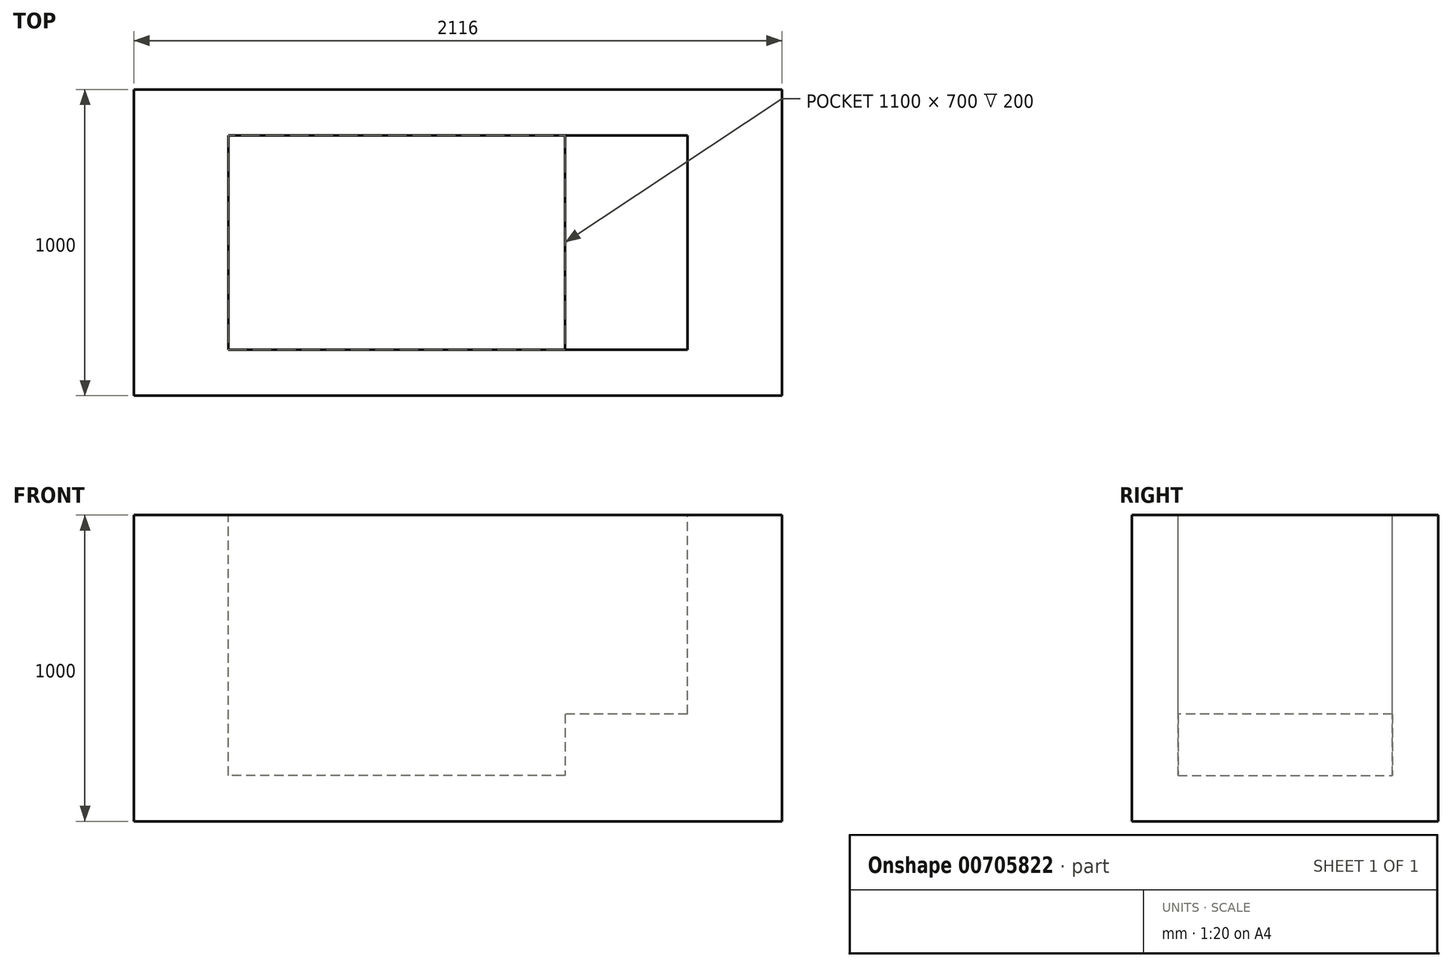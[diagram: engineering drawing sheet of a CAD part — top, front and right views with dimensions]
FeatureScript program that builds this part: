
annotation { "Feature Type Name" : "Feature", "Feature Type Description" : "" }
export const myFeature = defineFeature(function(context is Context, id is Id, definition is map)
    precondition{}
    {
        {
            var Q0;
            Q0=qCreatedBy(makeId("Top.planeOp"),FACE);
            var sketch = newSketch(context, id + "F0", { "sketchPlane" : qUnion([Q0])});
            skLineSegment(sketch, "E0.bottom", {"start": v(-110.6, -36.4) * mm, "end": v(2005.4, -36.4) * mm});
            skLineSegment(sketch, "E0.top", {"start": v(-110.6, 963.6) * mm, "end": v(2005.4, 963.6) * mm});
            skLineSegment(sketch, "E0.left", {"start": v(-110.6, -36.4) * mm, "end": v(-110.6, 963.6) * mm});
            skLineSegment(sketch, "E0.right", {"start": v(2005.4, -36.4) * mm, "end": v(2005.4, 963.6) * mm});
            skSolve(sketch);
        }
        {
            var Q0;
            Q0=makeQuery(id+"F0.imprint","IMPRINT",FACE,{"disambiguationData":[TD([[makeQuery(id+"F0.imprint","IMPRINT",EDGE,{"derivedFrom":sQuery(id+"F0.wireOp",EDGE,"E0.bottom")}),1.0]])]});
            extrude(context, id + "F1", {"entities" : qUnion([Q0]), "depth" : 1000 * mm, "offsetDistance" : 25 * mm});
        }
        {
            var Q0;
            Q0=makeQuery(id+"F1.opExtrude","CAP_FACE",FACE,{"disambiguationData":[OSD([sQuery(id+"F0.wireOp",EDGE,"E0.bottom"),sQuery(id+"F0.wireOp",EDGE,"E0.top"),sQuery(id+"F0.wireOp",EDGE,"E0.left"),sQuery(id+"F0.wireOp",EDGE,"E0.right")])],"isStart":false});
            var sketch = newSketch(context, id + "F2", { "sketchPlane" : qUnion([Q0])});
            skLineSegment(sketch, "E1.bottom", {"start": v(1697.4, 813.6) * mm, "end": v(197.4, 813.6) * mm});
            skLineSegment(sketch, "E1.top", {"start": v(1697.4, 113.6) * mm, "end": v(197.4, 113.6) * mm});
            skLineSegment(sketch, "E1.left", {"start": v(1697.4, 813.6) * mm, "end": v(1697.4, 113.6) * mm});
            skLineSegment(sketch, "E1.right", {"start": v(197.4, 813.6) * mm, "end": v(197.4, 113.6) * mm});
            skSolve(sketch);
        }
        {
            var Q0;
            Q0=makeQuery(id+"F2.imprint","IMPRINT",FACE,{"disambiguationData":[TD([[makeQuery(id+"F2.imprint","IMPRINT",EDGE,{"derivedFrom":sQuery(id+"F2.wireOp",EDGE,"E1.bottom")}),1.0]])]});
            extrude(context, id + "F3", {"entities" : qUnion([Q0]), "operationType" : NewBodyOperationType.REMOVE, "oppositeDirection" : true, "depth" : 850 * mm, "offsetDistance" : 25 * mm});
        }
        {
            var Q0;
            Q0=makeQuery(id+"F3.boolean.opBoolean","COPY",FACE,{"derivedFrom":makeQuery(id+"F3.opExtrude","CAP_FACE",FACE,{"disambiguationData":[OSD([sQuery(id+"F2.wireOp",EDGE,"E1.bottom"),sQuery(id+"F2.wireOp",EDGE,"E1.top"),sQuery(id+"F2.wireOp",EDGE,"E1.left"),sQuery(id+"F2.wireOp",EDGE,"E1.right")])],"isStart":false})});
            var sketch = newSketch(context, id + "F4", { "sketchPlane" : qUnion([Q0])});
            skLineSegment(sketch, "E2.bottom", {"start": v(1697.4, 113.6) * mm, "end": v(1297.4, 113.6) * mm});
            skLineSegment(sketch, "E2.top", {"start": v(1697.4, 813.6) * mm, "end": v(1297.4, 813.6) * mm});
            skLineSegment(sketch, "E2.left", {"start": v(1697.4, 113.6) * mm, "end": v(1697.4, 813.6) * mm});
            skLineSegment(sketch, "E2.right", {"start": v(1297.4, 113.6) * mm, "end": v(1297.4, 813.6) * mm});
            skSolve(sketch);
        }
        {
            var Q0;
            Q0=makeQuery(id+"F4.imprint","IMPRINT",FACE,{"disambiguationData":[TD([[makeQuery(id+"F4.imprint","IMPRINT",EDGE,{"derivedFrom":sQuery(id+"F4.wireOp",EDGE,"E2.bottom")}),-1.0]])]});
            extrude(context, id + "F5", {"entities" : qUnion([Q0]), "operationType" : NewBodyOperationType.ADD, "depth" : 200 * mm, "offsetDistance" : 25 * mm});
        }
    });
